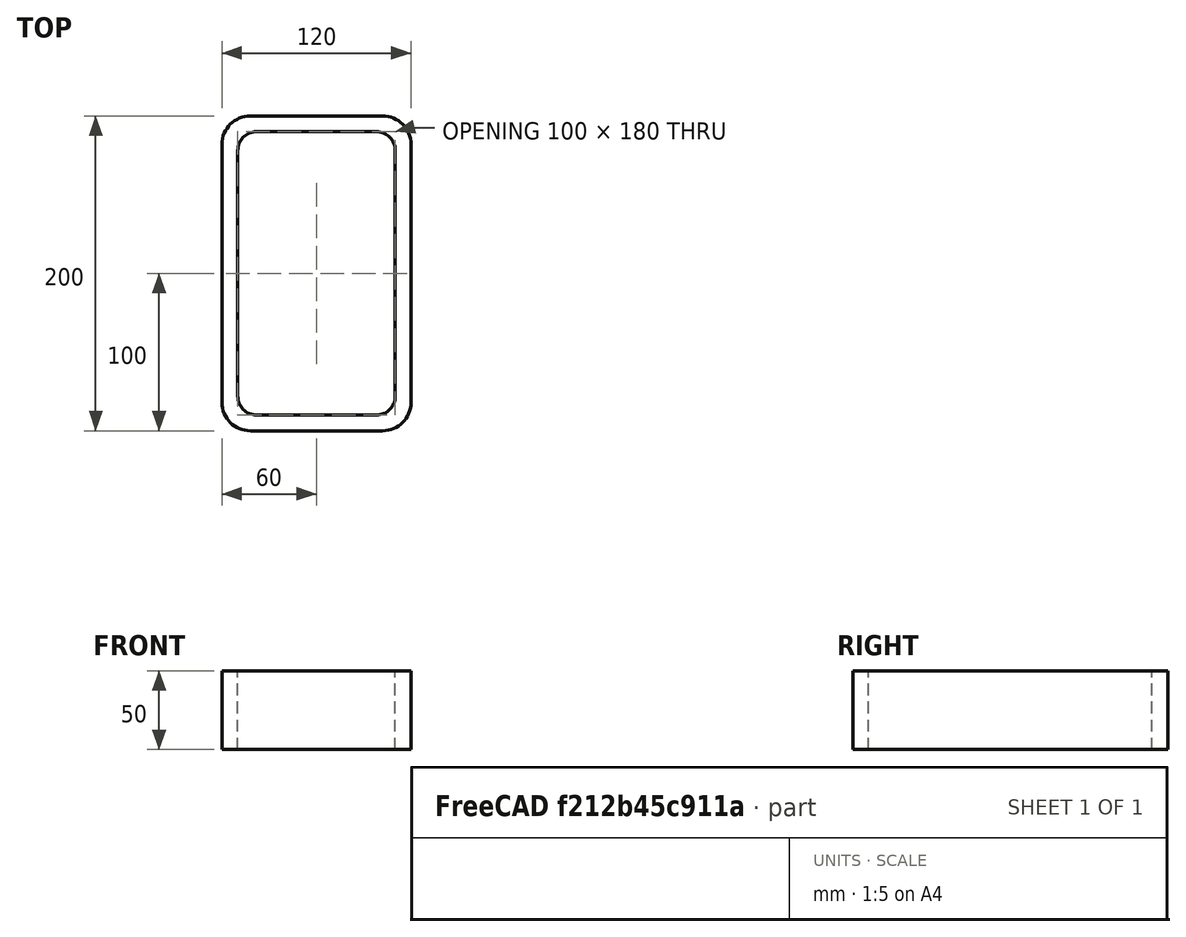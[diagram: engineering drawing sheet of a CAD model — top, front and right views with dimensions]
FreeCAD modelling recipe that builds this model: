
FCSTD DOCUMENT  (FreeCAD 0.15R4671 (Git))
Label: Rectangular hollow section 200x120x10 EN10219 S235JRH
License: All rights reserved
LicenseURL: http://en.wikipedia.org/wiki/All_rights_reserved
objects: Sketcher::SketchObject×1, Part::Extrusion×1
note: 2 computed .brp shape members not serialized (recipe doc carries the construction recipe); baked Part::Feature solids carry a one-line shape summary decoded from their .brp

FEATURE [Sketcher::SketchObject] Sketch
  sketch-geometry (16):
    g0: LineSegment StartX=-38 StartY=90 StartZ=0 EndX=38 EndY=90 EndZ=0
    g1: LineSegment StartX=50 StartY=78 StartZ=0 EndX=50 EndY=-78 EndZ=0
    g2: LineSegment StartX=38 StartY=-90 StartZ=0 EndX=-38 EndY=-90 EndZ=0
    g3: LineSegment StartX=-50 StartY=-78 StartZ=0 EndX=-50 EndY=78 EndZ=0
    g4: LineSegment StartX=-42 StartY=100 StartZ=0 EndX=42 EndY=100 EndZ=0
    g5: LineSegment StartX=60 StartY=82 StartZ=0 EndX=60 EndY=-82 EndZ=0
    g6: LineSegment StartX=42 StartY=-100 StartZ=0 EndX=-42 EndY=-100 EndZ=0
    g7: LineSegment StartX=-60 StartY=-82 StartZ=0 EndX=-60 EndY=82 EndZ=0
    g8: ArcOfCircle CenterX=-38 CenterY=78 CenterZ=0 NormalX=0 NormalY=0 NormalZ=1 Radius=12 StartAngle=1.5708 EndAngle=3.14159
    g9: ArcOfCircle CenterX=38 CenterY=78 CenterZ=0 NormalX=0 NormalY=0 NormalZ=1 Radius=12 StartAngle=0 EndAngle=1.5708
    g10: ArcOfCircle CenterX=38 CenterY=-78 CenterZ=0 NormalX=0 NormalY=0 NormalZ=1 Radius=12 StartAngle=4.71239 EndAngle=6.28319
    g11: ArcOfCircle CenterX=-38 CenterY=-78 CenterZ=0 NormalX=0 NormalY=0 NormalZ=1 Radius=12 StartAngle=3.14159 EndAngle=4.71239
    g12: ArcOfCircle CenterX=42 CenterY=82 CenterZ=0 NormalX=0 NormalY=0 NormalZ=1 Radius=18 StartAngle=0 EndAngle=1.5708
    g13: ArcOfCircle CenterX=42 CenterY=-82 CenterZ=0 NormalX=0 NormalY=0 NormalZ=1 Radius=18 StartAngle=4.71239 EndAngle=6.28319
    g14: ArcOfCircle CenterX=-42 CenterY=-82 CenterZ=0 NormalX=0 NormalY=0 NormalZ=1 Radius=18 StartAngle=3.14159 EndAngle=4.71239
    g15: ArcOfCircle CenterX=-42 CenterY=82 CenterZ=0 NormalX=0 NormalY=0 NormalZ=1 Radius=18 StartAngle=1.5708 EndAngle=3.14159
  constraints (36):
    c: Horizontal(g2)
    c: Vertical(g3)
    c: Horizontal(g6)
    c: Vertical(g7)
    c: Tangent(g3,g8) = 1.5708
    c: Tangent(g0,g8) = 1.5708
    c: Tangent(g0,g9) = 1.5708
    c: Tangent(g1,g9) = 1.5708
    c: Tangent(g1,g10) = 1.5708
    c: Tangent(g2,g10) = 1.5708
    c: Tangent(g2,g11) = 1.5708
    c: Tangent(g3,g11) = 1.5708
    c: Tangent(g4,g12) = 1.5708
    c: Tangent(g5,g12) = 1.5708
    c: Tangent(g5,g13) = 1.5708
    c: Tangent(g6,g13) = 1.5708
    c: Tangent(g6,g14) = 1.5708
    c: Tangent(g7,g14) = 1.5708
    c: Tangent(g7,g15) = 1.5708
    c: Tangent(g4,g15) = 1.5708
    c: Equal(g9,g8)
    c: Equal(g9,g11)
    c: Equal(g9,g10)
    c: Equal(g12,g15)
    c: Equal(g12,g14)
    c: Equal(g12,g13)
    c: Symmetric(g4,g6,g-1)
    c: Symmetric(g7,g5,g-2)
    c: DistanceY(g4,g6) = -200
    c: DistanceX(g7,g5) = 120
    c: Symmetric(g3,g1,g-2)
    c: Symmetric(g0,g2,g-1)
    c: DistanceY(g0,g4) = 10
    c: DistanceX(g5,g1) = -10
    c: Radius(g9) = 12
    c: Radius(g12) = 18
FEATURE [Part::Extrusion] Extrude  label="Rectangular hollow section 200x120x10 EN10219 S235JRH"
  Base = -> Sketch
  Dir = (0,0,50)
  Solid = true
